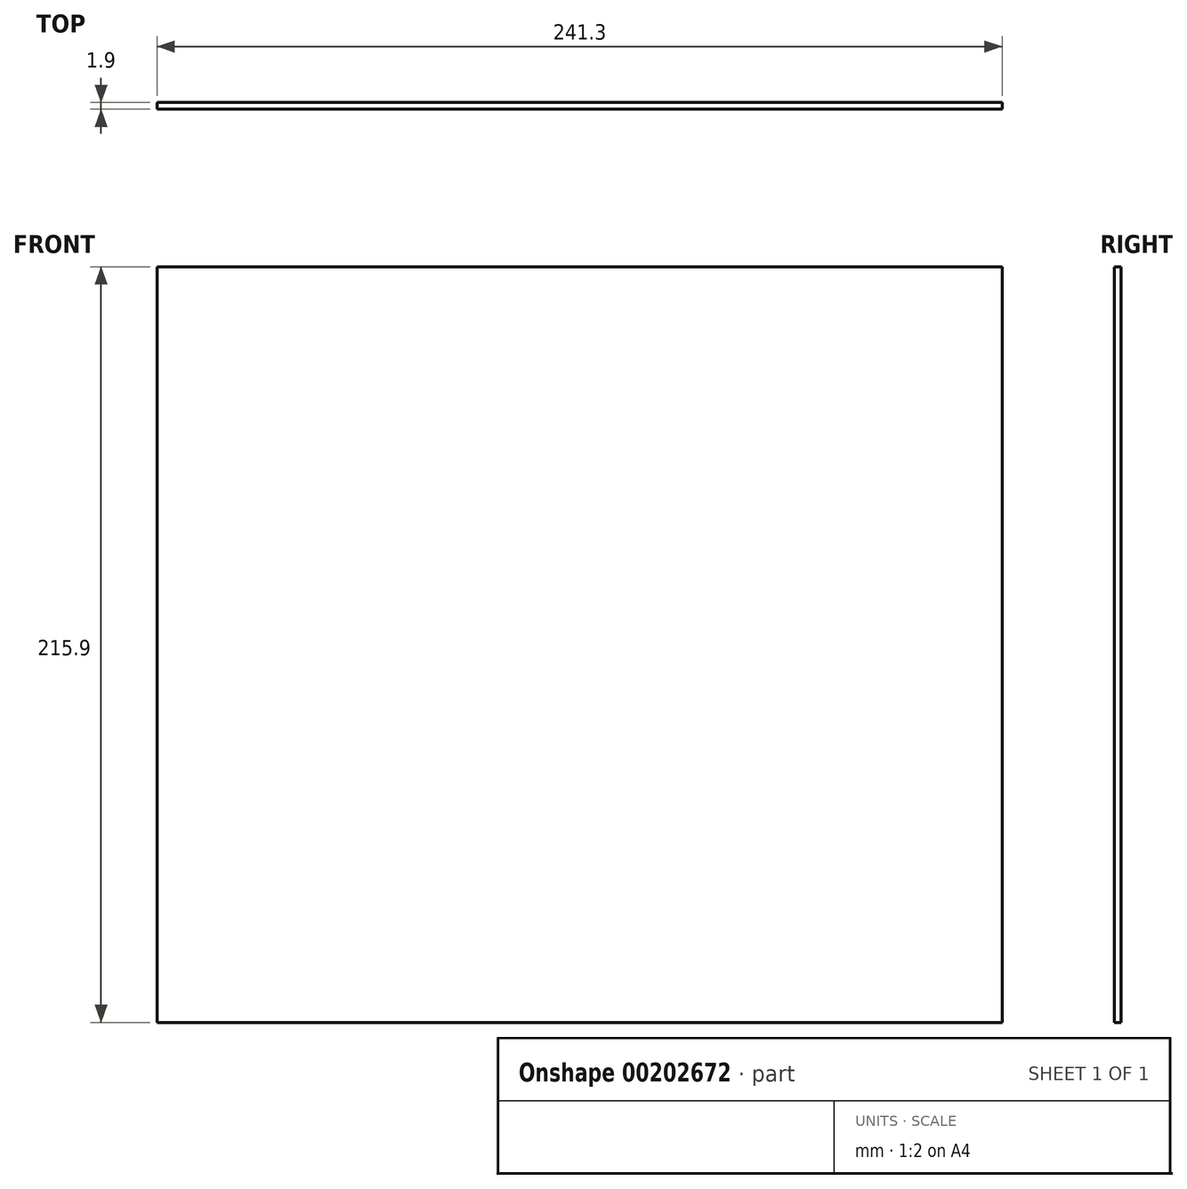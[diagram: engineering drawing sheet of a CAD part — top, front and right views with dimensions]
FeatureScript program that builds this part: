
annotation { "Feature Type Name" : "Feature", "Feature Type Description" : "" }
export const myFeature = defineFeature(function(context is Context, id is Id, definition is map)
    precondition{}
    {
        {
            var Q0;
            Q0=qCreatedBy(makeId("Front.planeOp"),FACE);
            var sketch = newSketch(context, id + "F0", { "sketchPlane" : qUnion([Q0])});
            skLineSegment(sketch, "E0.bottom", {"start": v(-120.65, 107.95) * mm, "end": v(120.65, 107.95) * mm});
            skLineSegment(sketch, "E0.top", {"start": v(-120.65, -107.95) * mm, "end": v(120.65, -107.95) * mm});
            skLineSegment(sketch, "E0.left", {"start": v(-120.65, 107.95) * mm, "end": v(-120.65, -107.95) * mm});
            skLineSegment(sketch, "E0.right", {"start": v(120.65, 107.95) * mm, "end": v(120.65, -107.95) * mm});
            skPoint(sketch, "E0.middle", {"position": v(0, 0) * mm});
            skSolve(sketch);
        }
        {
            var Q0;
            Q0 = qSketchRegion(id + "F0", true);
            extrude(context, id + "F1", {"entities" : qUnion([Q0]), "depth" : 1.9 * mm});
        }
    });
